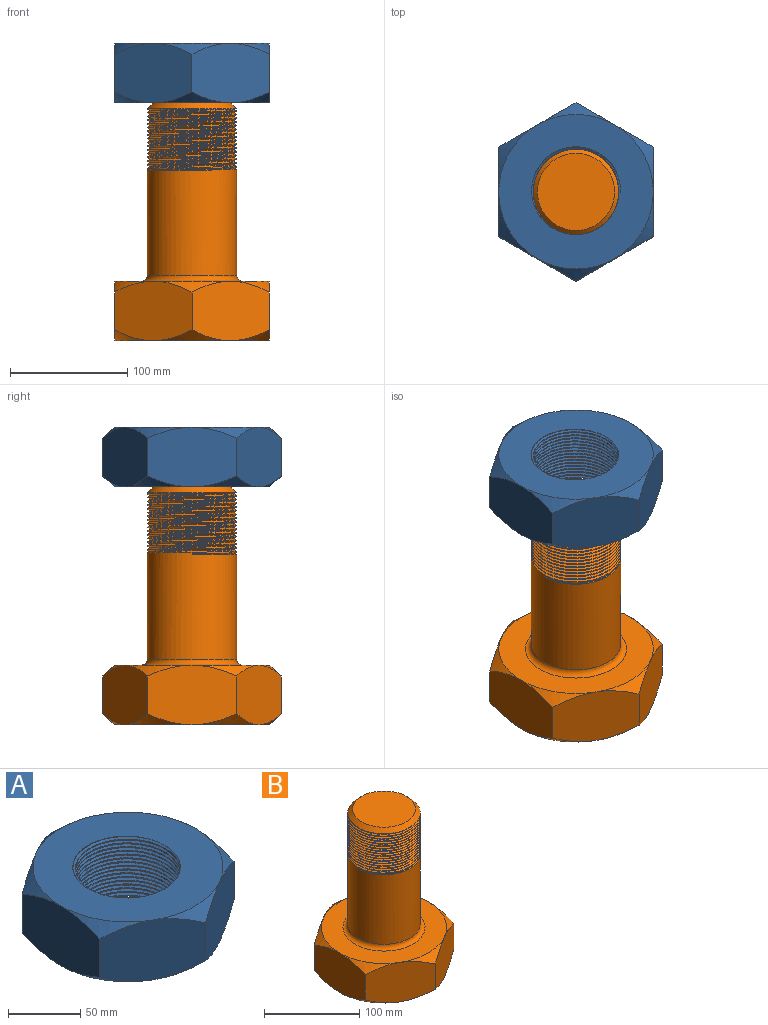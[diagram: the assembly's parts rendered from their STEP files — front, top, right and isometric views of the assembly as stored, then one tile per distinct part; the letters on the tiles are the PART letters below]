
ASSEMBLY  parts=2 mates=1
PART A: 24 faces, bbox 153x153.1x54 mm
  f0: plane 132.77x132.61mm, normal (0,0,-1), area 9346.1mm2, adj f2,f3,f4,f5,f6,f7,f8,f9
  f1: plane 132.61x132.61mm, normal (0,0,1), area 9315.3mm2, adj f14,f15,f16,f17,f18,f19,f20,f21
  f2: plane 66.03x50.83mm, normal (-0.5,-0.87,0), area 3394.9mm2, adj f0,f3,f7,f9,f10,f14,f15
  f3: plane 76.23x50.83mm, normal (-1,0,0), area 3394.9mm2, adj f0,f2,f4,f10,f11,f14,f16
  f4: plane 66.03x50.83mm, normal (-0.5,0.87,0), area 3394.9mm2, adj f0,f3,f5,f11,f12,f16,f17
  f5: plane 66.03x50.83mm, normal (0.5,0.87,0), area 3394.9mm2, adj f0,f4,f6,f12,f13,f17,f18
  f6: plane 76.23x50.83mm, normal (1,0,0), area 3394.9mm2, adj f0,f5,f7,f8,f13,f18,f19
  f7: plane 66.03x50.83mm, normal (0.5,-0.87,0), area 3394.9mm2, adj f0,f2,f6,f8,f9,f15,f19
  f8: cone r=83mm half-angle=48deg, axis (0,0,1), area 308.3mm2, adj f0,f6,f7
  f9: cone r=83mm half-angle=48deg, axis (0,0,1), area 308.3mm2, adj f0,f2,f7
  f10: cone r=83mm half-angle=48deg, axis (0,0,1), area 308.3mm2, adj f0,f2,f3
  f11: cone r=83mm half-angle=48deg, axis (0,0,1), area 308.3mm2, adj f0,f3,f4
  f12: cone r=83mm half-angle=48deg, axis (0,0,1), area 308.3mm2, adj f0,f4,f5
  f13: cone r=83mm half-angle=48deg, axis (0,0,1), area 308.3mm2, adj f0,f5,f6
  f14: cone r=83mm half-angle=48deg, axis (0,0,-1), area 315.2mm2, adj f1,f2,f3
  f15: cone r=83mm half-angle=48deg, axis (0,0,-1), area 315.2mm2, adj f1,f2,f7
  f16: cone r=83mm half-angle=48deg, axis (0,0,-1), area 315.2mm2, adj f1,f3,f4
  f17: cone r=83mm half-angle=48deg, axis (0,0,-1), area 315.2mm2, adj f1,f4,f5
  f18: cone r=83mm half-angle=48deg, axis (0,0,-1), area 315.2mm2, adj f1,f5,f6
  f19: cone r=83mm half-angle=48deg, axis (0,0,-1), area 315.2mm2, adj f1,f6,f7
  f20: bspline ~88.29x76.46mm, area 7477.6mm2, adj f0,f1,f22,f23
  f21: bspline ~88.29x76.46mm, area 7436.9mm2, adj f0,f1,f22,f23
  f22: bspline ~88.62x76.75mm, area 1775.2mm2, adj f0,f1,f20,f21
  f23: cylinder r=36.51mm len=73.03mm, axis (0,0,-1), area 906mm2, adj f0,f1,f20,f21
PART B: 48 faces, bbox 159.5x159.5x210.4 mm
  f0: plane 73.12x57.95mm, normal (-0.5,-0.87,0), area 3389.8mm2, adj f1,f5,f6,f7,f8,f9
  f1: plane 83.37x57.96mm, normal (-1,0,0), area 3389.8mm2, adj f0,f2,f6,f8,f10,f11
  f2: plane 73.12x57.95mm, normal (-0.5,0.87,0), area 3389.8mm2, adj f1,f3,f10,f11,f12,f13
  f3: plane 73.12x57.95mm, normal (0.5,0.87,0), area 3389.8mm2, adj f2,f4,f12,f13,f14,f15
  f4: plane 83.37x57.96mm, normal (1,0,0), area 3389.8mm2, adj f3,f5,f14,f15,f16,f17
  f5: plane 73.12x57.95mm, normal (0.5,-0.87,0), area 3389.8mm2, adj f0,f4,f7,f9,f16,f17
  f6: cone r=83.01mm half-angle=48deg, axis (0,0,1), area 499.4mm2, adj f0,f1,f18
  f7: cone r=83.01mm half-angle=48deg, axis (0,0,1), area 499.4mm2, adj f0,f5,f18
  f8: cone r=83.01mm half-angle=48deg, axis (0,0,-1), area 499.4mm2, adj f0,f1,f19
  f9: cone r=83.01mm half-angle=48deg, axis (0,0,-1), area 499.4mm2, adj f0,f5,f19
  f10: cone r=83.01mm half-angle=48deg, axis (0,0,1), area 499.4mm2, adj f1,f2,f18
  f11: cone r=83.01mm half-angle=48deg, axis (0,0,-1), area 499.4mm2, adj f1,f2,f19
  f12: cone r=83.01mm half-angle=48deg, axis (0,0,1), area 499.4mm2, adj f2,f3,f18
  f13: cone r=83.01mm half-angle=48deg, axis (0,0,-1), area 499.4mm2, adj f2,f3,f19
  f14: cone r=83.01mm half-angle=48deg, axis (0,0,1), area 499.4mm2, adj f3,f4,f18
  f15: cone r=83.01mm half-angle=48deg, axis (0,0,-1), area 499.4mm2, adj f3,f4,f19
  f16: cone r=83.01mm half-angle=48deg, axis (0,0,1), area 499.4mm2, adj f4,f5,f18
  f17: cone r=83.01mm half-angle=48deg, axis (0,0,-1), area 499.4mm2, adj f4,f5,f19
  f18: plane 131.98x131.98mm, normal (0,0,-1), area 13681.1mm2, adj f6,f7,f10,f12,f14,f16
  f19: plane 131.98x131.98mm, normal (0,0,1), area 7823.6mm2, adj f8,f9,f11,f13,f15,f17,f39
  f20: cylinder r=38.1mm len=94.62mm, axis (0,0,-1), area 21824.2mm2, adj f21,f39,f40,f41,f42,f45
  f21: cylinder r=38.1mm len=76.2mm, axis (0,0,-1), area 95.2mm2, adj f20,f22,f44,f45
  f22: cylinder r=38.1mm len=76.2mm, axis (0,0,-1), area 95.1mm2, adj f21,f23,f44,f45
  f23: cylinder r=38.1mm len=76.2mm, axis (0,0,-1), area 95mm2, adj f22,f24,f44,f45
  f24: cylinder r=38.1mm len=76.2mm, axis (0,0,-1), area 95.2mm2, adj f23,f25,f44,f45
  f25: cylinder r=38.1mm len=76.2mm, axis (0,0,-1), area 95.4mm2, adj f24,f26,f44,f45
  f26: cylinder r=38.1mm len=76.2mm, axis (0,0,-1), area 95.1mm2, adj f25,f27,f44,f45
  f27: cylinder r=38.1mm len=76.2mm, axis (0,0,-1), area 94.8mm2, adj f26,f28,f44,f45
  f28: cylinder r=38.1mm len=76.2mm, axis (0,0,-1), area 94.9mm2, adj f27,f29,f44,f45
  f29: cylinder r=38.1mm len=76.2mm, axis (0,0,-1), area 95mm2, adj f28,f30,f44,f45
  f30: cylinder r=38.1mm len=76.2mm, axis (0,0,-1), area 94.8mm2, adj f29,f31,f44,f45
  f31: cylinder r=38.1mm len=76.2mm, axis (0,0,-1), area 94.6mm2, adj f30,f32,f44,f45
  f32: cylinder r=38.1mm len=76.2mm, axis (0,0,-1), area 95mm2, adj f31,f33,f44,f45
  f33: cylinder r=38.1mm len=76.2mm, axis (0,0,-1), area 95.3mm2, adj f32,f34,f44,f45
  f34: cylinder r=38.1mm len=76.2mm, axis (0,0,-1), area 95.2mm2, adj f33,f35,f44,f45
  f35: cylinder r=38.1mm len=76.2mm, axis (0,0,-1), area 95mm2, adj f34,f36,f44,f45
  f36: cylinder r=38.1mm len=26.69mm, axis (0,0,-1), area 6mm2, adj f35,f38,f44
  f37: plane 66.04x66.04mm, normal (0,0,1), area 3425.3mm2, adj f38
  f38: cone r=33.02mm half-angle=45deg, axis (0,0,-1), area 1605.2mm2, adj f36,f37,f47
  f39: torus R=43.18mm, axis (0,0,1), area 2002.8mm2, adj f19,f20
  f40: plane 0.96x0.32mm, normal (0,-1,0), area 0.2mm2, adj f20,f41,f42,f46
  f41: bspline ~78.89x78.4mm, area 251.8mm2, adj f20,f40,f44,f46
  f42: bspline ~78.89x78.4mm, area 251.8mm2, adj f20,f40,f45,f46
  f43: bspline ~84.02x72.76mm, area 3145.6mm2, adj f44,f45,f46,f47
  f44: bspline ~87.99x76.2mm, area 7094.4mm2, adj f21,f22,f23,f24,f25,f26,f27,f28
  f45: bspline ~87.99x76.2mm, area 7331.1mm2, adj f20,f21,f22,f23,f24,f25,f26,f27
  f46: bspline ~75.43x74.93mm, area 207.1mm2, adj f40,f41,f42,f43
  f47: plane 77.23x77.23mm, normal (0,0,-1), area 233.8mm2, adj f38,f43,f44,f45
PLACE A t=(-92.09,13.06,200.94)mm
PLACE B t=(-92.09,13.06,-2.26)mm fixed
MATE revolute A.f23 <-> B.f20  axis (0,0,-1) through (-92.09,13.06,200.94)mm
